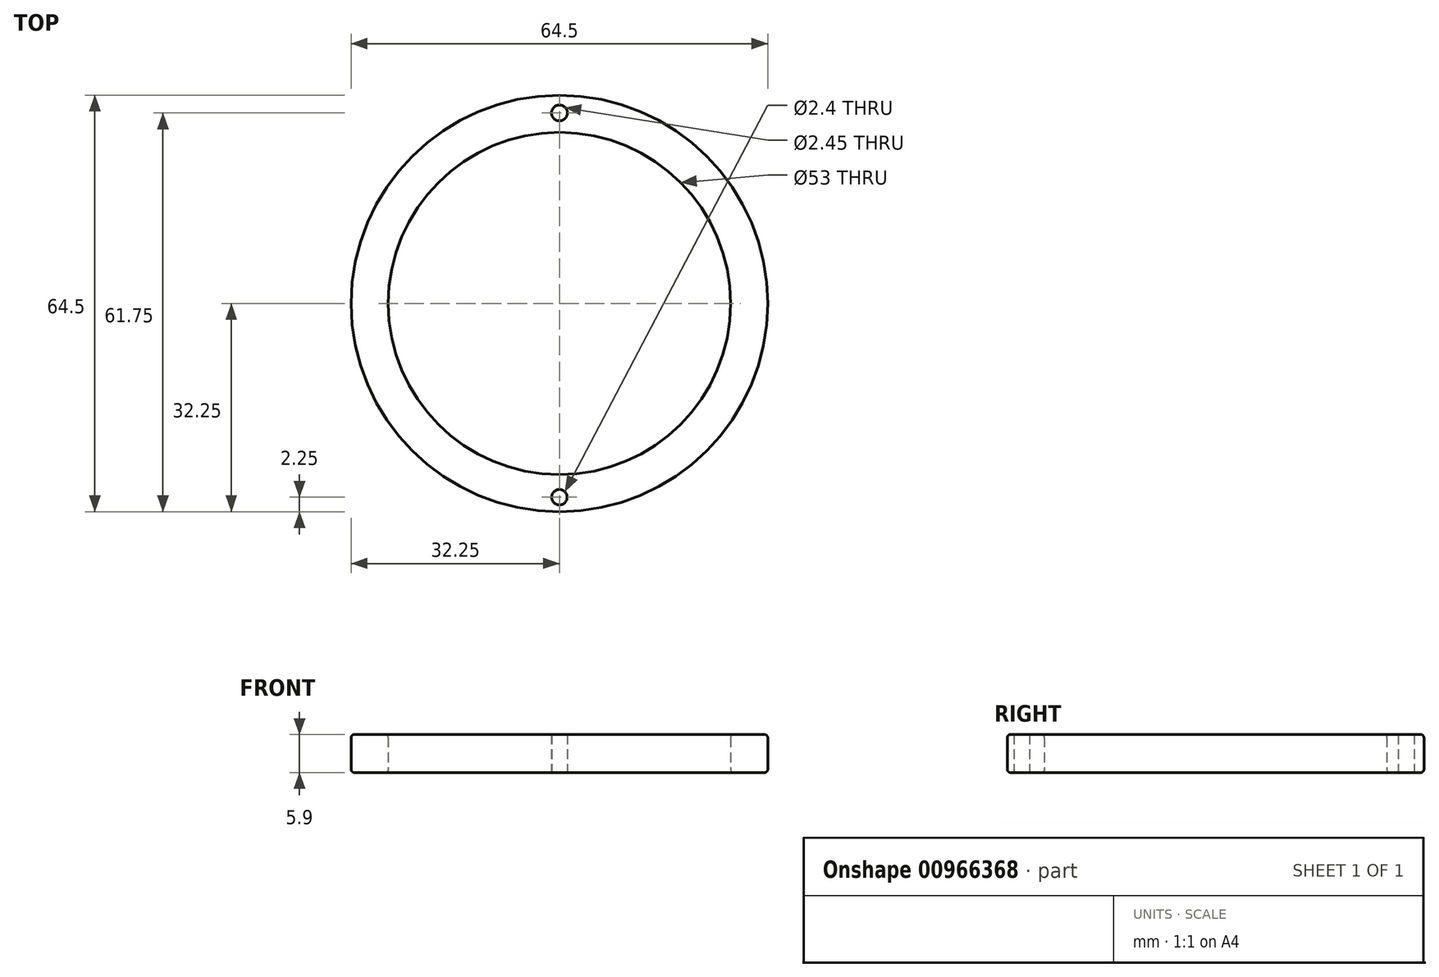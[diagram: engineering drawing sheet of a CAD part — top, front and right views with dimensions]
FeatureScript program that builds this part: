
annotation { "Feature Type Name" : "Feature", "Feature Type Description" : "" }
export const myFeature = defineFeature(function(context is Context, id is Id, definition is map)
    precondition{}
    {
        {
            var Q0;
            Q0=qCreatedBy(makeId("Top.planeOp"),FACE);
            var sketch = newSketch(context, id + "F0", { "sketchPlane" : qUnion([Q0])});
            skCircle(sketch, "E0", {"center": v(0, 0) * mm, "radius": 26.5 * mm});
            skCircle(sketch, "E1", {"center": v(0, 0) * mm, "radius": 32.25 * mm});
            skPoint(sketch, "E2", {"position": v(0, -30) * mm});
            skPoint(sketch, "E3.1.0", {"position": v(0, 29.5) * mm});
            skPoint(sketch, "E3.center", {"position": v(0, -0.25) * mm});
            skCircle(sketch, "E4", {"center": v(0, -30) * mm, "radius": 1.2 * mm});
            skCircle(sketch, "E5", {"center": v(0, 29.5) * mm, "radius": 1.13 * mm});
            skCircle(sketch, "E6", {"center": v(0, 29.5) * mm, "radius": 1.23 * mm});
            skCircle(sketch, "E7", {"center": v(0, 29.5) * mm, "radius": 1.2 * mm});
            skSolve(sketch);
        }
        {
            var Q0;
            Q0=qSketchRegion(id+"F0",true);
            extrude(context, id + "F1", {"entities" : qUnion([Q0]), "depth" : 5 * mm, "offsetDistance" : 25 * mm});
        }
        {
            var Q0;
            Q0=qSketchRegion(id+"F0",true);
            extrude(context, id + "F2", {"entities" : qUnion([Q0]), "operationType" : NewBodyOperationType.ADD, "depth" : 5.9 * mm, "offsetDistance" : 25 * mm});
        }
        {
            var Q0;
            Q0=makeQuery(id+"F1.opExtrude","CAP_EDGE",EDGE,{"disambiguationData":[OSD([sQuery(id+"F0.wireOp",EDGE,"E0")])],"isStart":true});
            var Q1;
            Q1=makeQuery(id+"F1.opExtrude","CAP_EDGE",EDGE,{"disambiguationData":[OSD([sQuery(id+"F0.wireOp",EDGE,"E1")])],"isStart":true});
            var Q2;
            Q2=makeQuery(id+"F1.opExtrude","CAP_EDGE",EDGE,{"disambiguationData":[OSD([sQuery(id+"F0.wireOp",EDGE,"E1")])],"isStart":false});
            fillet(context, id + "F3", {"entities" : qUnion([Q0, Q1, Q2]), "radius" : .5 * mm, "tangentPropagation" : true, "allowEdgeOverflow" : false});
        }
        {
            var Q0;
            Q0=makeQuery(id+"F2.opExtrude","CAP_EDGE",EDGE,{"disambiguationData":[OSD([sQuery(id+"F0.wireOp",EDGE,"E0")])],"isStart":false});
            var Q1;
            Q1=makeQuery(id+"F2.opExtrude","CAP_EDGE",EDGE,{"disambiguationData":[OSD([sQuery(id+"F0.wireOp",EDGE,"E1")])],"isStart":false});
            fillet(context, id + "F4", {"entities" : qUnion([Q0, Q1]), "radius" : .5 * mm, "tangentPropagation" : true, "allowEdgeOverflow" : false});
        }
    });
